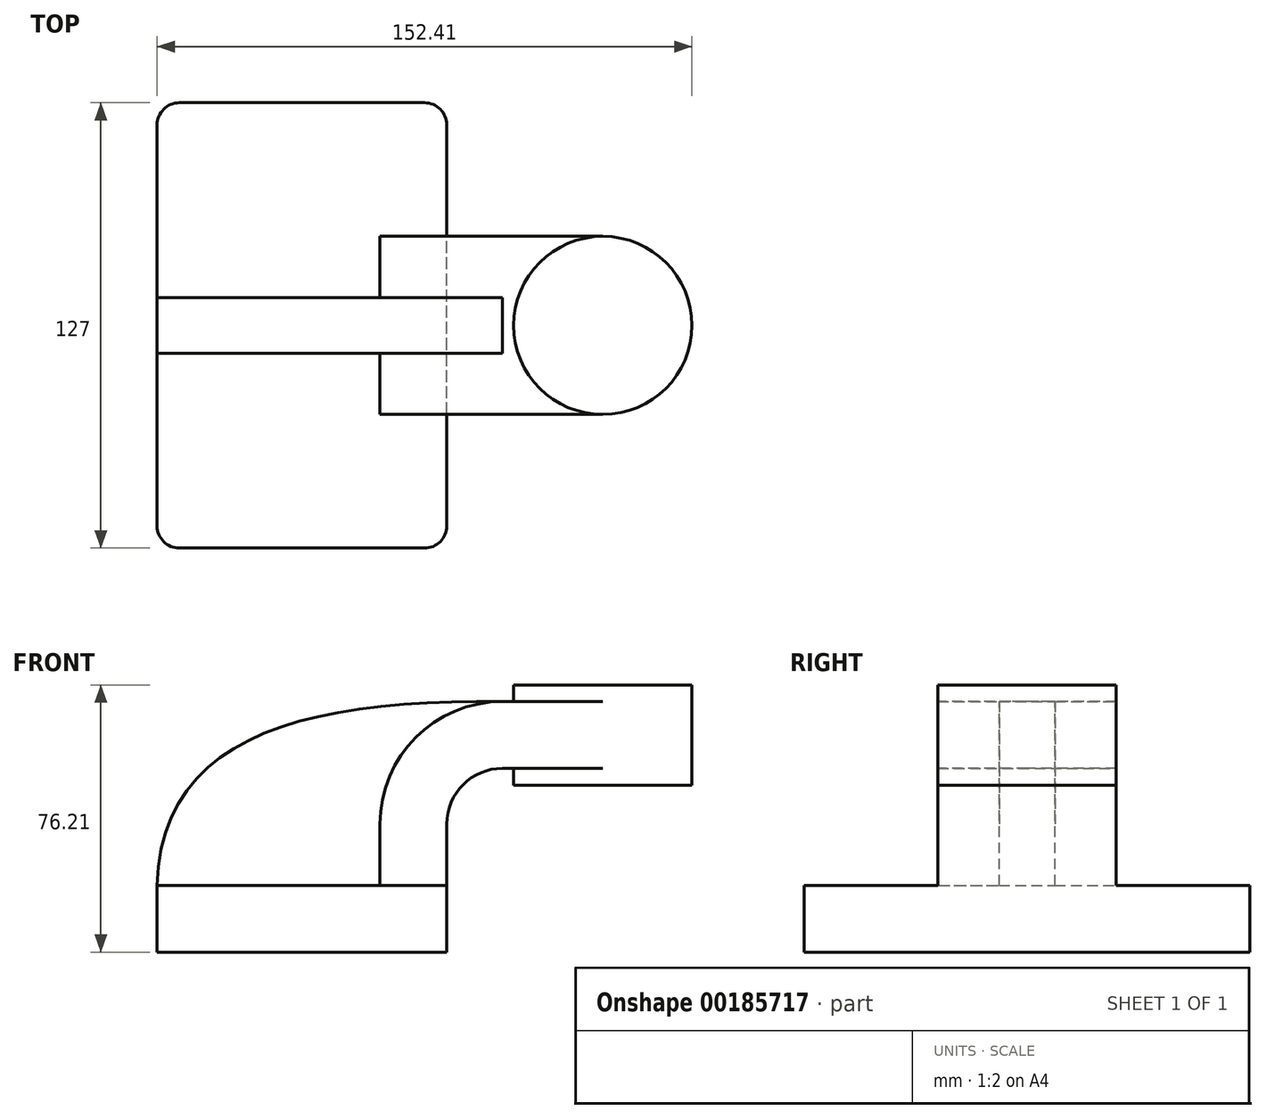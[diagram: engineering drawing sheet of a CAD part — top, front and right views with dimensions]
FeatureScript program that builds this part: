
annotation { "Feature Type Name" : "Feature", "Feature Type Description" : "" }
export const myFeature = defineFeature(function(context is Context, id is Id, definition is map)
    precondition{}
    {
        {
            var Q0;
            Q0=qCreatedBy(makeId("Front.planeOp"),FACE);
            var sketch = newSketch(context, id + "F0", { "sketchPlane" : qUnion([Q0])});
            skLineSegment(sketch, "E0.bottom", {"start": v(-41.28, 9.52) * mm, "end": v(41.27, 9.53) * mm});
            skLineSegment(sketch, "E0.top", {"start": v(-41.28, -9.53) * mm, "end": v(41.28, -9.53) * mm});
            skLineSegment(sketch, "E0.left", {"start": v(-41.28, 9.52) * mm, "end": v(-41.28, -9.53) * mm});
            skLineSegment(sketch, "E0.right", {"start": v(41.27, 9.53) * mm, "end": v(41.28, -9.52) * mm});
            skPoint(sketch, "E0.middle", {"position": v(0, 0) * mm});
            skLineSegment(sketch, "E1.bottom", {"start": v(111.13, 38.1) * mm, "end": v(60.33, 38.1) * mm});
            skLineSegment(sketch, "E1.top", {"start": v(111.13, 66.68) * mm, "end": v(60.33, 66.68) * mm});
            skLineSegment(sketch, "E1.left", {"start": v(111.13, 38.1) * mm, "end": v(111.13, 66.68) * mm});
            skLineSegment(sketch, "E1.right", {"start": v(60.33, 38.1) * mm, "end": v(60.33, 66.68) * mm});
            skPoint(sketch, "E1.middle", {"position": v(85.73, 52.39) * mm});
            skLineSegment(sketch, "E2", {"start": v(41.27, 9.53) * mm, "end": v(41.27, 27) * mm});
            skArc(sketch, "E3", {"start": v(57.15, 42.88) * mm, "mid": v(45.92, 38.23) * mm, "end": v(41.27, 27) * mm});
            skLineSegment(sketch, "E4", {"start": v(57.15, 42.88) * mm, "end": v(85.72, 42.88) * mm});
            skLineSegment(sketch, "E5.0", {"start": v(57.15, 61.93) * mm, "end": v(85.72, 61.93) * mm});
            skArc(sketch, "E5.1", {"start": v(57.15, 61.93) * mm, "mid": v(32.45, 51.7) * mm, "end": v(22.22, 27) * mm});
            skLineSegment(sketch, "E5.2", {"start": v(22.22, 9.53) * mm, "end": v(22.22, 27) * mm});
            skLineSegment(sketch, "E6", {"start": v(85.73, 38.1) * mm, "end": v(85.73, 66.68) * mm});
            skFitSpline(sketch, "E7", {"points": [v(-41.28, 9.52) * mm, v(57.15, 61.93) * mm], "startDerivative": vector(3.42, 126.96) * mm, "endDerivative": vector(171.45, -2.1) * mm});
            skSolve(sketch);
        }
        {
            var Q0;
            Q0=makeQuery(id+"F0.imprint","IMPRINT",FACE,{"disambiguationData":[TD([[makeQuery(id+"F0.imprint","IMPRINT",EDGE,{"derivedFrom":sQuery(id+"F0.wireOp",EDGE,"E0.top")}),1.0]])]});
            extrude(context, id + "F1", {"entities" : qUnion([Q0]), "endBound" : BoundingType.SYMMETRIC, "depth" : 127 * mm});
        }
        {
            var Q0;
            {var subQ1=sQuery(id+"F0.wireOp",EDGE,"E2");Q0=makeQuery(id+"F0.imprint","IMPRINT",FACE,{"disambiguationData":[TD([[makeQuery(id+"F0.imprint","IMPRINT",EDGE,{"derivedFrom":subQ1}),1.0]])]});}
            extrude(context, id + "F2", {"entities" : qUnion([Q0]), "operationType" : NewBodyOperationType.ADD, "endBound" : BoundingType.SYMMETRIC, "depth" : 50.8 * mm});
        }
        {
            var Q0;
            {var subQ0=sQuery(id+"F0.wireOp",EDGE,"E4");var subQ1=sQuery(id+"F0.wireOp",EDGE,"E1.right");var subQ2=makeQuery(id+"F0.imprint","INTERSECT",VERTEX,{"derivedFrom":[subQ1,subQ0]});Q0=makeQuery(id+"F0.imprint","IMPRINT",FACE,{"disambiguationData":[TD([[makeQuery(id+"F0.imprint","IMPRINT",EDGE,{"disambiguationData":[TD([[subQ2,-1.0]])],"derivedFrom":subQ1}),-1.0]])]});}
            extrude(context, id + "F3", {"entities" : qUnion([Q0]), "operationType" : NewBodyOperationType.ADD, "endBound" : BoundingType.SYMMETRIC, "depth" : 50.8 * mm});
        }
        {
            var Q0;
            Q0=makeQuery(id+"F0.imprint","IMPRINT",FACE,{"disambiguationData":[TD([[makeQuery(id+"F0.imprint","IMPRINT",EDGE,{"derivedFrom":sQuery(id+"F0.wireOp",EDGE,"E5.1")}),-1.0]])]});
            extrude(context, id + "F4", {"entities" : qUnion([Q0]), "operationType" : NewBodyOperationType.ADD, "endBound" : BoundingType.SYMMETRIC, "depth" : 15.88 * mm});
        }
        {
            var Q0;
            {var subQ0=sQuery(id+"F0.wireOp",EDGE,"E1.left");Q0=makeQuery(id+"F0.imprint","IMPRINT",FACE,{"disambiguationData":[TD([[makeQuery(id+"F0.imprint","IMPRINT",EDGE,{"derivedFrom":subQ0}),1.0]])]});}
            var Q1;
            Q1=sQuery(id+"F0.wireOp",EDGE,"E6");
            revolve(context, id + "F5", {"operationType" : NewBodyOperationType.ADD, "entities" : qUnion([Q0]), "axis" : qUnion([Q1]), "revolveType" : RevolveType.FULL});
        }
        {
            var Q0;
            Q0=makeQuery(id+"F1.opExtrude","CAP_EDGE",EDGE,{"disambiguationData":[OSD([sQuery(id+"F0.wireOp",EDGE,"E0.right")])],"isStart":false});
            var Q1;
            Q1=makeQuery(id+"F1.opExtrude","CAP_EDGE",EDGE,{"disambiguationData":[OSD([sQuery(id+"F0.wireOp",EDGE,"E0.left")])],"isStart":false});
            var Q2;
            Q2=makeQuery(id+"F1.opExtrude","CAP_EDGE",EDGE,{"disambiguationData":[OSD([sQuery(id+"F0.wireOp",EDGE,"E0.right")])],"isStart":true});
            var Q3;
            Q3=makeQuery(id+"F1.opExtrude","CAP_EDGE",EDGE,{"disambiguationData":[OSD([sQuery(id+"F0.wireOp",EDGE,"E0.left")])],"isStart":true});
            fillet(context, id + "F6", {"entities" : qUnion([Q0, Q1, Q2, Q3]), "radius" : 6.35 * mm, "tangentPropagation" : true, "allowEdgeOverflow" : false});
        }
    });
